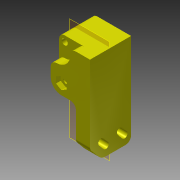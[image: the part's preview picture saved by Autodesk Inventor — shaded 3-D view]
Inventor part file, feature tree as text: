
AUTODESK INVENTOR PART (.ipt)
format: ipt  version: 2013 (Build 170138000, 138)  size: 227,328 bytes
history: native  units: in
note: dims shown in document units (in); Inventor stores cm internally (conversion verified against a paired STEP export)
features: extrude x9, sketch x9, reference x3, plane x1, mirror x1, fillet x1, projected_geometry x1
ambient origin geometry x8: Origin, YZ Plane, XZ Plane, XY Plane, X Axis, Y Axis, Z Axis, Center Point
bodies: Solid1 (feature_tree)
feature tree (25):
  extrude  "Extrusion1"  Depth=0.1969in
  extrude  "Extrusion2"  Depth=0.8661in TaperAngle=0.0deg
  plane  "Work Plane1"
  extrude  "Extrusion3"  Depth=0.1772in TaperAngle=0.0deg
  extrude  "Extrusion4"  Depth=0.9843in
  mirror  "Mirror1"
  extrude  "Extrusion5"  Depth=0.0354in
  extrude  "Extrusion6"  Depth=0.0354in TaperAngle=0.0deg
  extrude  "Extrusion7"  Depth=0.1181in TaperAngle=0.0deg
  extrude  "Extrusion8"  Depth=0.0984in TaperAngle=0.0deg
  extrude  "Extrusion9"  Depth=0.0984in TaperAngle=0.0deg
  fillet  "Fillet1"  Radius=0.1969in
  sketch  "Sketch1"  dims[d1=0.2953in d2=0.1969in]
  reference  "Reference1"
  reference  "Reference2"
  sketch  "Sketch2"  dims[d3=0.2362in d4=0.8661in d5=0.0in]
  sketch  "Sketch3"  dims[d6=0.5906in d8=0.1772in d9=0.0in]
  sketch  "Sketch4"  dims[d10=-0.4331in d11=0.9843in]
  sketch  "Sketch5"  dims[d14=0.3543in d15=0.0in d16=0.0354in d17=-0.3092in]
  sketch  "Sketch6"  dims[d18=0.126in d21=0.0354in d22=0.0in]
  sketch  "Sketch7"  dims[d23=0.2362in d25=0.1181in d26=0.0in]
  sketch  "Sketch8"  dims[d27=0.2224in d28=0.0984in d29=0.0in]
  reference  "Reference3"
  sketch  "Sketch9"  dims[d30=0.1181in d31=0.0984in d32=0.0in d33=0.1969in d36=0.0984in d37=0.0in d38=0.1181in d39=0.1181in]
  projected_geometry  "Project Cut Edges1"
